# Revit family: Lectern-Middle_Atlantic-L5_Series2
name_source: partatom
category: Furniture Systems
revit_build: Autodesk Revit MEP 2012 (Build: 20110916_2132(x64)
units: mm (PartAtom-declared; Revit-internal decimal feet)

## types (9) — shared parameters
Date Last Modified = June 5, 2013
Description = See Part Description
Equipment Abbreviation = LSL
Family Version = 1.0.0
Height = 47.75 "
Manufacturer = Middle Atlantic Products
Model = See Part Number
Model Disclaimer = For More Information, Contact Middle Atlantic
Product Documentation Link = http://www2.middleatlantic.com
Product Material = Steel - Middle Atlantic
Product Page URL = http://www.middleatlantic.com
Provide Feedback = https://www.surveymonkey.com
Rack Spaces RU = 12
URL = www.middleatlantic.com
zero-valued in all types: Cost

## per-type parameters (varying)
| type | Depth | Width | zz Integer 1 |
| 43" Traditional, Turret | 31.07 " | 45.14 " | 8 |
| 43" Contemporary, Turret | 31 " | 46.25 " | 7 |
| 43" Traditional, Flat | 31.07 " | 45.14 " | 9 |
| 33" Contemporary, Turret | 31 " | 36.25 " | 4 |
| 23" Contemporary, Turret | 31 " | 26.68 " | 1 |
| 33" Traditional, Flat | 31.07 " | 35.14 " | 6 |
| 23" Traditional, Flat | 31.07 " | 24.46 " | 3 |
| 33" Traditional, Turret | 31.07 " | 35.14 " | 5 |
| 23" Traditional, Turret | 31.07 " | 24.46 " | 2 |

## geometry (parser evidence)
native form markers: Blend x2, Sweep x3
no freeform markers — native parametric forms only
